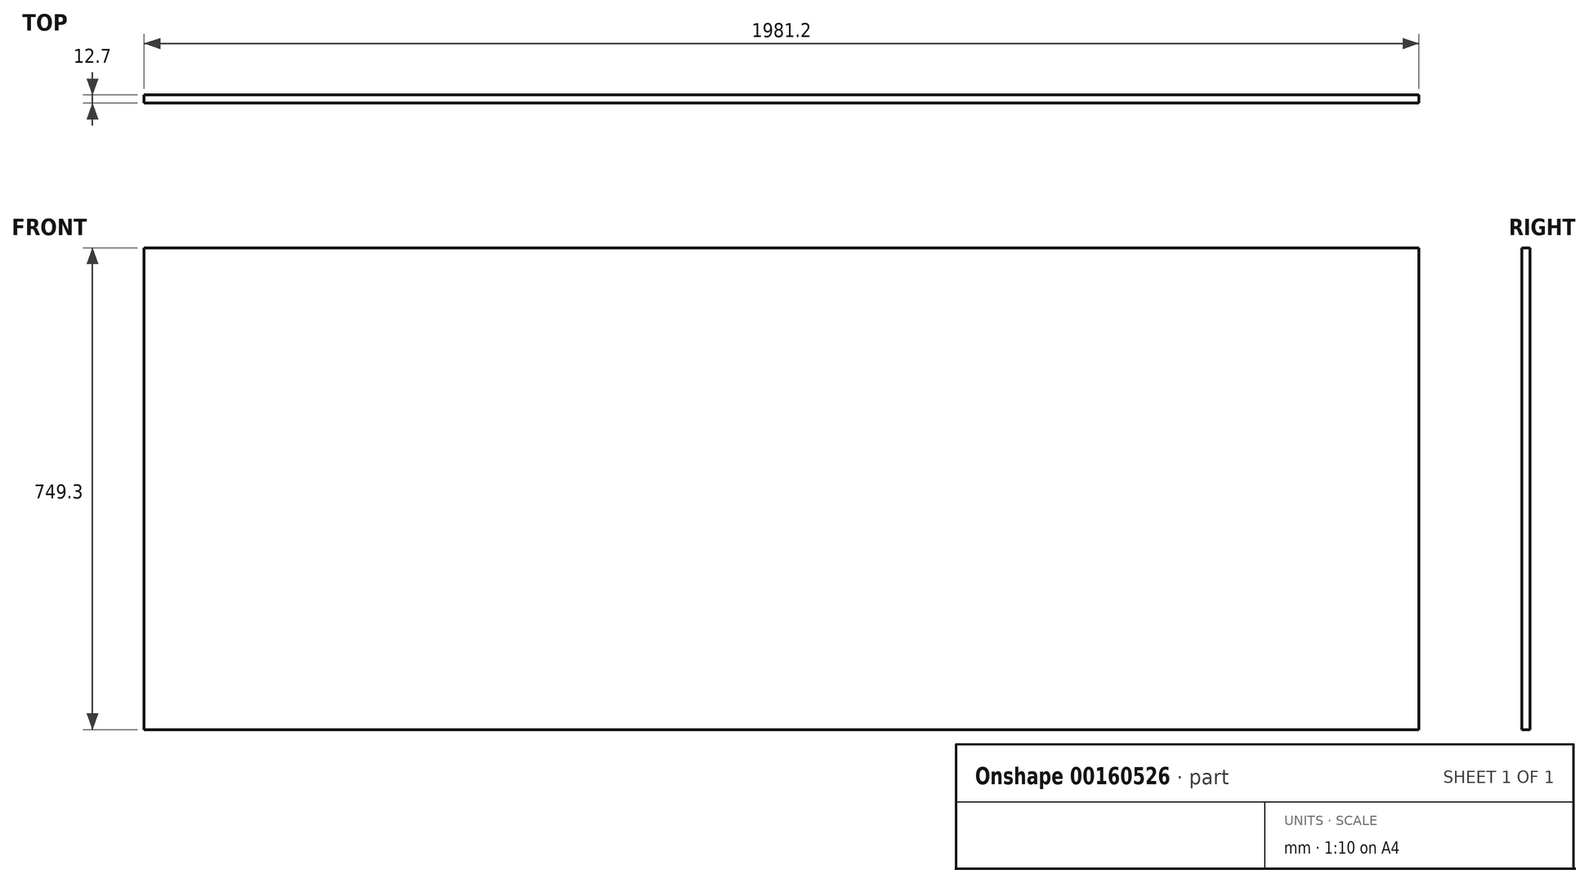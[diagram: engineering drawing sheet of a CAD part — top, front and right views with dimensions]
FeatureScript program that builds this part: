
annotation { "Feature Type Name" : "Feature", "Feature Type Description" : "" }
export const myFeature = defineFeature(function(context is Context, id is Id, definition is map)
    precondition{}
    {
        {
            var Q0;
            Q0=qCreatedBy(makeId("Front.planeOp"),FACE);
            var sketch = newSketch(context, id + "F0", { "sketchPlane" : qUnion([Q0])});
            skLineSegment(sketch, "E0.bottom", {"start": v(-1001.75, 415.05) * mm, "end": v(979.45, 415.05) * mm});
            skLineSegment(sketch, "E0.top", {"start": v(-1001.75, -334.25) * mm, "end": v(979.45, -334.25) * mm});
            skLineSegment(sketch, "E0.left", {"start": v(-1001.75, 415.05) * mm, "end": v(-1001.75, -334.25) * mm});
            skLineSegment(sketch, "E0.right", {"start": v(979.45, 415.05) * mm, "end": v(979.45, -334.25) * mm});
            skSolve(sketch);
        }
        {
            var Q0;
            Q0 = qSketchRegion(id + "F0", true);
            extrude(context, id + "F1", {"entities" : qUnion([Q0]), "depth" : 12.7 * mm});
        }
    });
